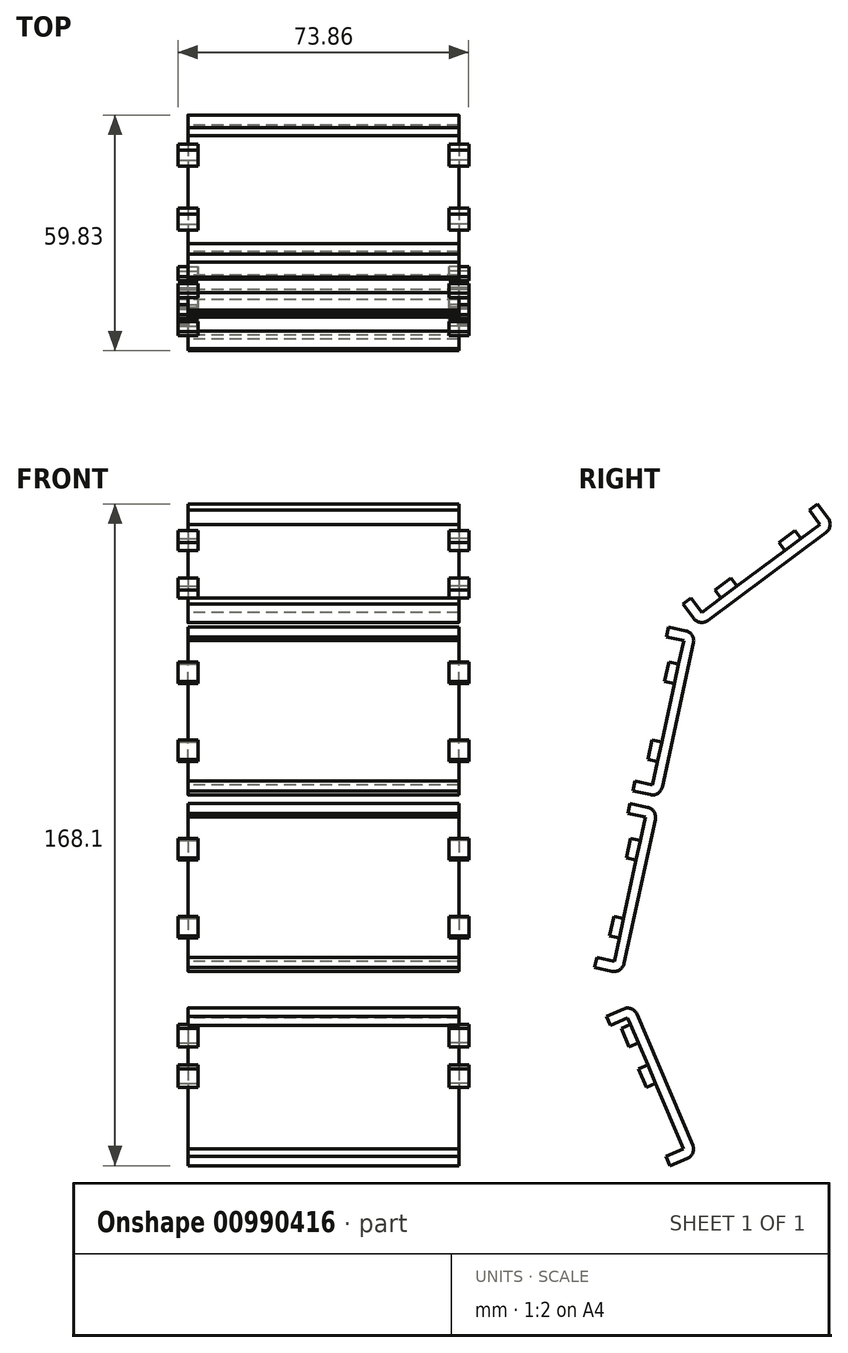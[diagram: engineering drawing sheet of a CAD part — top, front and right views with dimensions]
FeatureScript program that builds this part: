
annotation { "Feature Type Name" : "Feature", "Feature Type Description" : "" }
export const myFeature = defineFeature(function(context is Context, id is Id, definition is map)
    precondition{}
    {
        {
            var Q0;
            Q0=qCreatedBy(makeId("Right.planeOp"),FACE);
            var sketch = newSketch(context, id + "F0", { "sketchPlane" : qUnion([Q0])});
            skLineSegment(sketch, "E0", {"start": v(0, 0) * mm, "end": v(0, 169.34) * mm});
            skLineSegment(sketch, "E1", {"start": v(0, 169.34) * mm, "end": v(200.4, 169.34) * mm});
            skLineSegment(sketch, "E2", {"start": v(0, 0) * mm, "end": v(43.05, 0) * mm, "construction": true});
            skLineSegment(sketch, "E3", {"start": v(43.05, 0) * mm, "end": v(23.47, 45.96) * mm});
            skLineSegment(sketch, "E4", {"start": v(0, 47.82) * mm, "end": v(22.68, 47.82) * mm, "construction": true});
            skLineSegment(sketch, "E5", {"start": v(22.68, 47.82) * mm, "end": v(22.68, 0) * mm, "construction": true});
            skLineSegment(sketch, "E6", {"start": v(23.1, 49.8) * mm, "end": v(40.9, 132) * mm});
            skLineSegment(sketch, "E7", {"start": v(41.4, 134.33) * mm, "end": v(0, 134.33) * mm, "construction": true});
            skLineSegment(sketch, "E8", {"start": v(41.4, 134.33) * mm, "end": v(43.05, 0) * mm, "construction": true});
            skLineSegment(sketch, "E9", {"start": v(43.31, 135.75) * mm, "end": v(72.51, 157.5) * mm});
            skLineSegment(sketch, "E10", {"start": v(74.2, 158.76) * mm, "end": v(74.2, 169.34) * mm, "construction": true});
            skLineSegment(sketch, "E11", {"start": v(74.2, 158.76) * mm, "end": v(0, 158.76) * mm, "construction": true});
            skPoint(sketch, "E12", {"position": v(100.2, 169.34) * mm});
            skLineSegment(sketch, "E13", {"start": v(100.2, 169.34) * mm, "end": v(100.2, 154.3) * mm, "construction": true});
            skLineSegment(sketch, "E14", {"start": v(76.3, 158.76) * mm, "end": v(100.2, 158.76) * mm});
            skLineSegment(sketch, "E15.4", {"start": v(41.18, -0.8) * mm, "end": v(20.56, 47.62) * mm, "construction": true});
            skLineSegment(sketch, "E15.5", {"start": v(20.56, 47.62) * mm, "end": v(39.58, 135.5) * mm});
            skLineSegment(sketch, "E15.6", {"start": v(39.58, 135.5) * mm, "end": v(73.52, 160.79) * mm});
            skLineSegment(sketch, "E15.7", {"start": v(73.52, 160.79) * mm, "end": v(100.2, 160.79) * mm});
            skLineSegment(sketch, "E16.5", {"start": v(11.62, 46.77) * mm, "end": v(31.89, 140.45) * mm});
            skLineSegment(sketch, "E16.6", {"start": v(31.89, 140.45) * mm, "end": v(70.69, 169.35) * mm, "construction": true});
            skLineSegment(sketch, "E16.7", {"start": v(70.69, 169.35) * mm, "end": v(100.2, 169.35) * mm});
            skLineSegment(sketch, "E17", {"start": v(31.89, 140.45) * mm, "end": v(38.14, 169.34) * mm, "construction": true});
            skLineSegment(sketch, "E18", {"start": v(10.6, 158.76) * mm, "end": v(0, 158.76) * mm, "construction": true});
            skLineSegment(sketch, "E19", {"start": v(10.6, 158.76) * mm, "end": v(10.6, 46.77) * mm});
            skLineSegment(sketch, "E20", {"start": v(10.6, 46.77) * mm, "end": v(11.62, 46.77) * mm});
            skLineSegment(sketch, "E21", {"start": v(36.3, 160.79) * mm, "end": v(31.89, 140.45) * mm, "construction": true});
            skLineSegment(sketch, "E22", {"start": v(41.4, 134.33) * mm, "end": v(48.98, 169.34) * mm, "construction": true});
            skLineSegment(sketch, "E23", {"start": v(47.13, 160.79) * mm, "end": v(44.8, 150.07) * mm});
            skLineSegment(sketch, "E24", {"start": v(13.2, 0) * mm, "end": v(0, 0) * mm});
            skLineSegment(sketch, "E25", {"start": v(31.54, 0) * mm, "end": v(43.05, 0) * mm});
            skLineSegment(sketch, "E26", {"start": v(100.2, 158.76) * mm, "end": v(100.2, 169.35) * mm});
            skPoint(sketch, "E27", {"position": v(46.69, 158.76) * mm});
            skPoint(sketch, "E28", {"position": v(56.47, 158.76) * mm});
            skLineSegment(sketch, "E29", {"start": v(46.69, 158.76) * mm, "end": v(56.47, 158.76) * mm});
            skLineSegment(sketch, "E30", {"start": v(44.8, 150.07) * mm, "end": v(46.69, 158.76) * mm});
            skLineSegment(sketch, "E31", {"start": v(10.6, 158.76) * mm, "end": v(35.85, 158.76) * mm});
            skLineSegment(sketch, "E32", {"start": v(35.85, 158.76) * mm, "end": v(31.89, 140.45) * mm});
            skLineSegment(sketch, "E33", {"start": v(44.8, 150.07) * mm, "end": v(56.47, 158.76) * mm});
            skLineSegment(sketch, "E34", {"start": v(30.88, 85.7) * mm, "end": v(20.53, 87.94) * mm, "construction": true});
            skLineSegment(sketch, "E35.0", {"start": v(33.3, -4.15) * mm, "end": v(12.94, 43.67) * mm, "construction": true});
            skLineSegment(sketch, "E36", {"start": v(22.68, 47.82) * mm, "end": v(18.8, 29.9) * mm, "construction": true});
            skLineSegment(sketch, "E37", {"start": v(18.8, 29.9) * mm, "end": v(12.34, 0) * mm});
            skLineSegment(sketch, "E38", {"start": v(18.8, 29.9) * mm, "end": v(31.54, 0) * mm});
            skLineSegment(sketch, "E39", {"start": v(12.34, 0) * mm, "end": v(31.54, 0) * mm});
            skLineSegment(sketch, "E40", {"start": v(20.56, 47.62) * mm, "end": v(40.84, 0) * mm});
            skPoint(sketch, "E41.visualSharp", {"position": v(41.4, 134.33) * mm});
            skArc(sketch, "E41.filletArc", {"start": v(43.31, 135.75) * mm, "mid": v(41.77, 134.1) * mm, "end": v(40.9, 132) * mm});
            skPoint(sketch, "E42.visualSharp", {"position": v(22.68, 47.82) * mm});
            skArc(sketch, "E42.filletArc", {"start": v(23.1, 49.8) * mm, "mid": v(23, 47.85) * mm, "end": v(23.47, 45.96) * mm});
            skPoint(sketch, "E43.visualSharp", {"position": v(74.2, 158.76) * mm});
            skArc(sketch, "E43.filletArc", {"start": v(76.3, 158.76) * mm, "mid": v(74.3, 158.44) * mm, "end": v(72.51, 157.5) * mm});
            skPoint(sketch, "E44", {"position": v(21.75, 93.6) * mm});
            skLineSegment(sketch, "E45", {"start": v(21.75, 93.6) * mm, "end": v(22.1, 95.21) * mm});
            skLineSegment(sketch, "E46", {"start": v(22.1, 95.21) * mm, "end": v(26.54, 94.25) * mm});
            skLineSegment(sketch, "E47", {"start": v(29.56, 96.2) * mm, "end": v(37.5, 132.86) * mm});
            skLineSegment(sketch, "E48", {"start": v(35.55, 135.88) * mm, "end": v(31.1, 136.84) * mm});
            skPoint(sketch, "E49.visualSharp", {"position": v(38.03, 135.35) * mm});
            skArc(sketch, "E49.filletArc", {"start": v(37.5, 132.86) * mm, "mid": v(37.15, 134.78) * mm, "end": v(35.55, 135.88) * mm});
            skPoint(sketch, "E50.visualSharp", {"position": v(29.02, 93.72) * mm});
            skArc(sketch, "E50.filletArc", {"start": v(26.54, 94.25) * mm, "mid": v(28.45, 94.6) * mm, "end": v(29.56, 96.2) * mm});
            skLineSegment(sketch, "E51", {"start": v(21.75, 93.6) * mm, "end": v(32.1, 91.37) * mm, "construction": true});
            skLineSegment(sketch, "E52.0", {"start": v(35.01, 133.4) * mm, "end": v(30.57, 134.36) * mm});
            skLineSegment(sketch, "E52.1", {"start": v(22.64, 97.7) * mm, "end": v(27.08, 96.74) * mm});
            skLineSegment(sketch, "E52.2", {"start": v(27.08, 96.74) * mm, "end": v(27.08, 96.74) * mm});
            skLineSegment(sketch, "E52.3", {"start": v(27.08, 96.74) * mm, "end": v(35.01, 133.4) * mm});
            skLineSegment(sketch, "E52.4", {"start": v(35.01, 133.4) * mm, "end": v(35.01, 133.4) * mm});
            skLineSegment(sketch, "E53.MirrorCS", {"start": v(21.4, 92) * mm, "end": v(25.85, 91.04) * mm});
            skArc(sketch, "E54.MirrorCS", {"start": v(25.85, 91.04) * mm, "mid": v(27.44, 89.94) * mm, "end": v(27.8, 88.02) * mm});
            skLineSegment(sketch, "E55.MirrorCS", {"start": v(27.8, 88.02) * mm, "end": v(19.86, 51.36) * mm});
            skArc(sketch, "E56.MirrorCS", {"start": v(19.86, 51.36) * mm, "mid": v(18.75, 49.76) * mm, "end": v(16.84, 49.41) * mm});
            skLineSegment(sketch, "E57.MirrorCS", {"start": v(16.84, 49.41) * mm, "end": v(12.4, 50.38) * mm});
            skLineSegment(sketch, "E58.MirrorCS", {"start": v(17.37, 51.9) * mm, "end": v(12.94, 52.86) * mm});
            skLineSegment(sketch, "E59.MirrorCS", {"start": v(25.3, 88.56) * mm, "end": v(17.37, 51.9) * mm});
            skLineSegment(sketch, "E60.MirrorCS", {"start": v(20.87, 89.52) * mm, "end": v(25.3, 88.56) * mm});
            skLineSegment(sketch, "E61", {"start": v(33.72, 127.42) * mm, "end": v(31.23, 127.96) * mm});
            skLineSegment(sketch, "E62", {"start": v(31.23, 127.96) * mm, "end": v(30.16, 123) * mm});
            skLineSegment(sketch, "E63", {"start": v(30.16, 123) * mm, "end": v(32.64, 122.46) * mm});
            skLineSegment(sketch, "E64", {"start": v(28.37, 102.7) * mm, "end": v(25.88, 103.24) * mm});
            skLineSegment(sketch, "E65", {"start": v(25.88, 103.24) * mm, "end": v(26.96, 108.2) * mm});
            skLineSegment(sketch, "E66", {"start": v(26.96, 108.2) * mm, "end": v(29.44, 107.66) * mm});
            skLineSegment(sketch, "E67.MirrorCS", {"start": v(24.02, 82.6) * mm, "end": v(21.54, 83.13) * mm});
            skLineSegment(sketch, "E68.MirrorCS", {"start": v(21.54, 83.13) * mm, "end": v(20.46, 78.17) * mm});
            skLineSegment(sketch, "E69.MirrorCS", {"start": v(20.46, 78.17) * mm, "end": v(22.94, 77.63) * mm});
            skLineSegment(sketch, "E70.MirrorCS", {"start": v(17.26, 63.37) * mm, "end": v(19.74, 62.84) * mm});
            skLineSegment(sketch, "E71.MirrorCS", {"start": v(16.19, 58.4) * mm, "end": v(17.26, 63.37) * mm});
            skLineSegment(sketch, "E72.MirrorCS", {"start": v(18.67, 57.87) * mm, "end": v(16.19, 58.4) * mm});
            skLineSegment(sketch, "E73", {"start": v(31.89, 140.45) * mm, "end": v(41.4, 134.33) * mm, "construction": true});
            skLineSegment(sketch, "E74.MirrorCS", {"start": v(37.56, 139.02) * mm, "end": v(34.85, 142.66) * mm});
            skArc(sketch, "E75.MirrorCS", {"start": v(41.12, 138.5) * mm, "mid": v(39.23, 138.02) * mm, "end": v(37.56, 139.02) * mm});
            skLineSegment(sketch, "E76.MirrorCS", {"start": v(71.2, 160.9) * mm, "end": v(41.12, 138.5) * mm});
            skArc(sketch, "E77.MirrorCS", {"start": v(71.72, 164.46) * mm, "mid": v(72.2, 162.57) * mm, "end": v(71.2, 160.9) * mm});
            skLineSegment(sketch, "E78.MirrorCS", {"start": v(69, 168.1) * mm, "end": v(71.72, 164.46) * mm});
            skLineSegment(sketch, "E79.MirrorCS", {"start": v(66.97, 166.58) * mm, "end": v(69.69, 162.94) * mm});
            skLineSegment(sketch, "E80.MirrorCS", {"start": v(69.69, 162.94) * mm, "end": v(39.6, 140.53) * mm});
            skLineSegment(sketch, "E81.MirrorCS", {"start": v(64.8, 159.3) * mm, "end": v(63.28, 161.33) * mm});
            skLineSegment(sketch, "E82.MirrorCS", {"start": v(63.28, 161.33) * mm, "end": v(59.2, 158.3) * mm});
            skLineSegment(sketch, "E83.MirrorCS", {"start": v(59.2, 158.3) * mm, "end": v(60.72, 156.26) * mm});
            skLineSegment(sketch, "E84.MirrorCS", {"start": v(47.06, 149.26) * mm, "end": v(48.58, 147.22) * mm});
            skLineSegment(sketch, "E85.MirrorCS", {"start": v(42.99, 146.22) * mm, "end": v(47.06, 149.26) * mm});
            skLineSegment(sketch, "E86.MirrorCS", {"start": v(44.5, 144.19) * mm, "end": v(42.99, 146.22) * mm});
            skLineSegment(sketch, "E87.MirrorCS", {"start": v(39.6, 140.53) * mm, "end": v(36.89, 144.18) * mm});
            skLineSegment(sketch, "E88", {"start": v(70.69, 169.35) * mm, "end": v(70.69, 164.55) * mm});
            skLineSegment(sketch, "E89", {"start": v(68.15, 162) * mm, "end": v(0, 162) * mm});
            skPoint(sketch, "E90.visualSharp", {"position": v(70.69, 162) * mm});
            skArc(sketch, "E90.filletArc", {"start": v(68.15, 162) * mm, "mid": v(69.94, 162.75) * mm, "end": v(70.69, 164.55) * mm});
            skLineSegment(sketch, "E91.0", {"start": v(68.15, 164.55) * mm, "end": v(0, 164.55) * mm});
            skLineSegment(sketch, "E91.1", {"start": v(68.15, 169.63) * mm, "end": v(68.15, 164.55) * mm});
            skLineSegment(sketch, "E92", {"start": v(55.17, 164.55) * mm, "end": v(55.17, 167.09) * mm});
            skLineSegment(sketch, "E93", {"start": v(55.17, 167.09) * mm, "end": v(50.1, 167.09) * mm});
            skLineSegment(sketch, "E94", {"start": v(50.1, 167.09) * mm, "end": v(50.1, 164.55) * mm});
            skLineSegment(sketch, "E95", {"start": v(10.4, 164.55) * mm, "end": v(10.4, 167.09) * mm});
            skLineSegment(sketch, "E96", {"start": v(10.4, 167.09) * mm, "end": v(5.32, 167.09) * mm});
            skLineSegment(sketch, "E97", {"start": v(5.32, 167.09) * mm, "end": v(5.32, 164.55) * mm});
            skLineSegment(sketch, "E98", {"start": v(22.68, 47.82) * mm, "end": v(11.62, 46.77) * mm, "construction": true});
            skLineSegment(sketch, "E99", {"start": v(15.36, 37.97) * mm, "end": v(19.78, 39.85) * mm});
            skLineSegment(sketch, "E100", {"start": v(23.11, 38.51) * mm, "end": v(37.3, 5.2) * mm});
            skLineSegment(sketch, "E101", {"start": v(35.96, 1.87) * mm, "end": v(31.54, -0.01) * mm});
            skPoint(sketch, "E102.visualSharp", {"position": v(38.3, 2.87) * mm});
            skArc(sketch, "E102.filletArc", {"start": v(35.96, 1.87) * mm, "mid": v(37.32, 3.26) * mm, "end": v(37.3, 5.2) * mm});
            skPoint(sketch, "E103.visualSharp", {"position": v(22.12, 40.85) * mm});
            skArc(sketch, "E103.filletArc", {"start": v(23.11, 38.51) * mm, "mid": v(21.72, 39.87) * mm, "end": v(19.78, 39.85) * mm});
            skLineSegment(sketch, "E104.0", {"start": v(34.97, 4.2) * mm, "end": v(25.52, 0.18) * mm});
            skLineSegment(sketch, "E104.1", {"start": v(20.78, 37.52) * mm, "end": v(34.97, 4.2) * mm});
            skLineSegment(sketch, "E104.2", {"start": v(16.36, 35.63) * mm, "end": v(20.78, 37.52) * mm});
            skLineSegment(sketch, "E105", {"start": v(27.86, 20.9) * mm, "end": v(25.52, 19.9) * mm});
            skLineSegment(sketch, "E106", {"start": v(25.52, 19.9) * mm, "end": v(23.53, 24.57) * mm});
            skLineSegment(sketch, "E107", {"start": v(23.53, 24.57) * mm, "end": v(25.87, 25.57) * mm});
            skLineSegment(sketch, "E108", {"start": v(21.48, 35.85) * mm, "end": v(19.15, 34.86) * mm});
            skLineSegment(sketch, "E109", {"start": v(19.15, 34.86) * mm, "end": v(21.14, 30.18) * mm});
            skLineSegment(sketch, "E110", {"start": v(21.14, 30.18) * mm, "end": v(23.48, 31.18) * mm});
            skLineSegment(sketch, "E111", {"start": v(79.6, 169.35) * mm, "end": v(79.6, 164.55) * mm});
            skLineSegment(sketch, "E112", {"start": v(82.14, 162) * mm, "end": v(100.2, 162) * mm});
            skPoint(sketch, "E113.visualSharp", {"position": v(79.6, 162) * mm});
            skArc(sketch, "E113.filletArc", {"start": v(79.6, 164.55) * mm, "mid": v(80.34, 162.75) * mm, "end": v(82.14, 162) * mm});
            skLineSegment(sketch, "E114.0", {"start": v(82.14, 164.55) * mm, "end": v(100.2, 164.55) * mm});
            skLineSegment(sketch, "E114.1", {"start": v(82.14, 169.35) * mm, "end": v(82.14, 164.55) * mm});
            skLineSegment(sketch, "E115", {"start": v(84.57, 164.55) * mm, "end": v(84.57, 167.09) * mm});
            skPoint(sketch, "E115.endSnap0", {"position": v(68.15, 167.09) * mm});
            skLineSegment(sketch, "E116", {"start": v(84.57, 167.09) * mm, "end": v(89.65, 167.09) * mm});
            skLineSegment(sketch, "E117", {"start": v(89.65, 167.09) * mm, "end": v(89.65, 164.55) * mm});
            skLineSegment(sketch, "E118", {"start": v(34.85, 142.66) * mm, "end": v(36.89, 144.18) * mm});
            skLineSegment(sketch, "E119", {"start": v(66.97, 166.58) * mm, "end": v(69, 168.1) * mm});
            skLineSegment(sketch, "E120", {"start": v(15.36, 37.97) * mm, "end": v(16.36, 35.63) * mm});
            skSolve(sketch);
        }
        {
            var Q0;
            {var subQ0=sQuery(id+"F0.wireOp",EDGE,"E88");var subQ1=makeQuery(id+"F0.imprint","IMPRINT",VERTEX,{"derivedFrom":subQ0});Q0=makeQuery(id+"F0.imprint","IMPRINT",FACE,{"disambiguationData":[TD([[makeQuery(id+"F0.imprint","IMPRINT",EDGE,{"disambiguationData":[TD([[subQ1,1.0]])],"derivedFrom":subQ0}),-1.0]])]});}
            var Q1;
            {var subQ5=sQuery(id+"F0.wireOp",EDGE,"E46");Q1=makeQuery(id+"F0.imprint","IMPRINT",FACE,{"disambiguationData":[TD([[makeQuery(id+"F0.imprint","IMPRINT",EDGE,{"derivedFrom":subQ5}),1.0]])]});}
            var Q2;
            {var subQ7=sQuery(id+"F0.wireOp",EDGE,"E53.MirrorCS");Q2=makeQuery(id+"F0.imprint","IMPRINT",FACE,{"disambiguationData":[TD([[makeQuery(id+"F0.imprint","IMPRINT",EDGE,{"derivedFrom":subQ7}),-1.0]])]});}
            var Q3;
            Q3=makeQuery(id+"F0.imprint","IMPRINT",FACE,{"disambiguationData":[TD([[makeQuery(id+"F0.imprint","IMPRINT",EDGE,{"derivedFrom":sQuery(id+"F0.wireOp",EDGE,"E99")}),-1.0]])]});
            var Q4;
            Q4=makeQuery(id+"F0.imprint","IMPRINT",FACE,{"disambiguationData":[TD([[makeQuery(id+"F0.imprint","IMPRINT",EDGE,{"derivedFrom":sQuery(id+"F0.wireOp",EDGE,"E74.MirrorCS")}),-1.0]])]});
            var Q5;
            {var subQ3=sQuery(id+"F0.wireOp",EDGE,"E78.MirrorCS");var subQ11=sQuery(id+"F0.wireOp",EDGE,"E119");var subQ12=makeQuery(id+"F0.imprint","INTERSECT",VERTEX,{"derivedFrom":[subQ3,subQ11]});Q5=makeQuery(id+"F0.imprint","IMPRINT",FACE,{"disambiguationData":[TD([[makeQuery(id+"F0.imprint","IMPRINT",EDGE,{"disambiguationData":[TD([[subQ12,-1.0]])],"derivedFrom":subQ3}),-1.0]])]});}
            var Q6;
            {var subQ0=sQuery(id+"F0.wireOp",EDGE,"E119");var subQ1=sQuery(id+"F0.wireOp",EDGE,"E79.MirrorCS");var subQ2=makeQuery(id+"F0.imprint","INTERSECT",VERTEX,{"derivedFrom":[subQ1,subQ0]});Q6=makeQuery(id+"F0.imprint","IMPRINT",FACE,{"disambiguationData":[TD([[makeQuery(id+"F0.imprint","IMPRINT",EDGE,{"disambiguationData":[TD([[subQ2,-1.0]])],"derivedFrom":subQ1}),1.0]])]});}
            extrude(context, id + "F1", {"entities" : qUnion([Q0, Q1, Q2, Q3, Q4, Q5, Q6]), "endBound" : BoundingType.SYMMETRIC, "depth" : 68.78 * mm, "offsetDistance" : 25.4 * mm});
        }
        {
            var Q0;
            {var subQ0=sQuery(id+"F0.wireOp",EDGE,"E81.MirrorCS");Q0=makeQuery(id+"F0.imprint","IMPRINT",FACE,{"disambiguationData":[TD([[makeQuery(id+"F0.imprint","IMPRINT",EDGE,{"derivedFrom":subQ0}),1.0]])]});}
            var Q1;
            {var subQ0=sQuery(id+"F0.wireOp",EDGE,"E84.MirrorCS");Q1=makeQuery(id+"F0.imprint","IMPRINT",FACE,{"disambiguationData":[TD([[makeQuery(id+"F0.imprint","IMPRINT",EDGE,{"derivedFrom":subQ0}),-1.0]])]});}
            var Q2;
            {var subQ0=sQuery(id+"F0.wireOp",EDGE,"E61");Q2=makeQuery(id+"F0.imprint","IMPRINT",FACE,{"disambiguationData":[TD([[makeQuery(id+"F0.imprint","IMPRINT",EDGE,{"derivedFrom":subQ0}),1.0]])]});}
            var Q3;
            {var subQ0=sQuery(id+"F0.wireOp",EDGE,"E64");Q3=makeQuery(id+"F0.imprint","IMPRINT",FACE,{"disambiguationData":[TD([[makeQuery(id+"F0.imprint","IMPRINT",EDGE,{"derivedFrom":subQ0}),-1.0]])]});}
            var Q4;
            {var subQ0=sQuery(id+"F0.wireOp",EDGE,"E70.MirrorCS");Q4=makeQuery(id+"F0.imprint","IMPRINT",FACE,{"disambiguationData":[TD([[makeQuery(id+"F0.imprint","IMPRINT",EDGE,{"derivedFrom":subQ0}),-1.0]])]});}
            var Q5;
            {var subQ0=sQuery(id+"F0.wireOp",EDGE,"E67.MirrorCS");Q5=makeQuery(id+"F0.imprint","IMPRINT",FACE,{"disambiguationData":[TD([[makeQuery(id+"F0.imprint","IMPRINT",EDGE,{"derivedFrom":subQ0}),1.0]])]});}
            var Q6;
            {var subQ0=sQuery(id+"F0.wireOp",EDGE,"E108");Q6=makeQuery(id+"F0.imprint","IMPRINT",FACE,{"disambiguationData":[TD([[makeQuery(id+"F0.imprint","IMPRINT",EDGE,{"derivedFrom":subQ0}),1.0]])]});}
            var Q7;
            {var subQ0=sQuery(id+"F0.wireOp",EDGE,"E105");Q7=makeQuery(id+"F0.imprint","IMPRINT",FACE,{"disambiguationData":[TD([[makeQuery(id+"F0.imprint","IMPRINT",EDGE,{"derivedFrom":subQ0}),-1.0]])]});}
            extrude(context, id + "F2", {"entities" : qUnion([Q0, Q1, Q2, Q3, Q4, Q5, Q6, Q7]), "operationType" : NewBodyOperationType.ADD, "depth" : 36.93 * mm, "offsetDistance" : 25.4 * mm, "hasSecondDirection" : true, "secondDirectionOppositeDirection" : true, "secondDirectionDepth" : -31.85 * mm});
        }
        {
            var Q0;
            {var subQ0=sQuery(id+"F0.wireOp",EDGE,"E81.MirrorCS");Q0=makeQuery(id+"F0.imprint","IMPRINT",FACE,{"disambiguationData":[TD([[makeQuery(id+"F0.imprint","IMPRINT",EDGE,{"derivedFrom":subQ0}),1.0]])]});}
            var Q1;
            {var subQ0=sQuery(id+"F0.wireOp",EDGE,"E84.MirrorCS");Q1=makeQuery(id+"F0.imprint","IMPRINT",FACE,{"disambiguationData":[TD([[makeQuery(id+"F0.imprint","IMPRINT",EDGE,{"derivedFrom":subQ0}),-1.0]])]});}
            var Q2;
            {var subQ0=sQuery(id+"F0.wireOp",EDGE,"E61");Q2=makeQuery(id+"F0.imprint","IMPRINT",FACE,{"disambiguationData":[TD([[makeQuery(id+"F0.imprint","IMPRINT",EDGE,{"derivedFrom":subQ0}),1.0]])]});}
            var Q3;
            {var subQ0=sQuery(id+"F0.wireOp",EDGE,"E64");Q3=makeQuery(id+"F0.imprint","IMPRINT",FACE,{"disambiguationData":[TD([[makeQuery(id+"F0.imprint","IMPRINT",EDGE,{"derivedFrom":subQ0}),-1.0]])]});}
            var Q4;
            {var subQ0=sQuery(id+"F0.wireOp",EDGE,"E67.MirrorCS");Q4=makeQuery(id+"F0.imprint","IMPRINT",FACE,{"disambiguationData":[TD([[makeQuery(id+"F0.imprint","IMPRINT",EDGE,{"derivedFrom":subQ0}),1.0]])]});}
            var Q5;
            {var subQ0=sQuery(id+"F0.wireOp",EDGE,"E70.MirrorCS");Q5=makeQuery(id+"F0.imprint","IMPRINT",FACE,{"disambiguationData":[TD([[makeQuery(id+"F0.imprint","IMPRINT",EDGE,{"derivedFrom":subQ0}),-1.0]])]});}
            var Q6;
            {var subQ0=sQuery(id+"F0.wireOp",EDGE,"E105");Q6=makeQuery(id+"F0.imprint","IMPRINT",FACE,{"disambiguationData":[TD([[makeQuery(id+"F0.imprint","IMPRINT",EDGE,{"derivedFrom":subQ0}),-1.0]])]});}
            var Q7;
            {var subQ0=sQuery(id+"F0.wireOp",EDGE,"E108");Q7=makeQuery(id+"F0.imprint","IMPRINT",FACE,{"disambiguationData":[TD([[makeQuery(id+"F0.imprint","IMPRINT",EDGE,{"derivedFrom":subQ0}),1.0]])]});}
            extrude(context, id + "F3", {"entities" : qUnion([Q0, Q1, Q2, Q3, Q4, Q5, Q6, Q7]), "operationType" : NewBodyOperationType.ADD, "depth" : -36.93 * mm, "offsetDistance" : 25.4 * mm, "hasSecondDirection" : true, "secondDirectionOppositeDirection" : true, "secondDirectionDepth" : 31.85 * mm});
        }
    });
